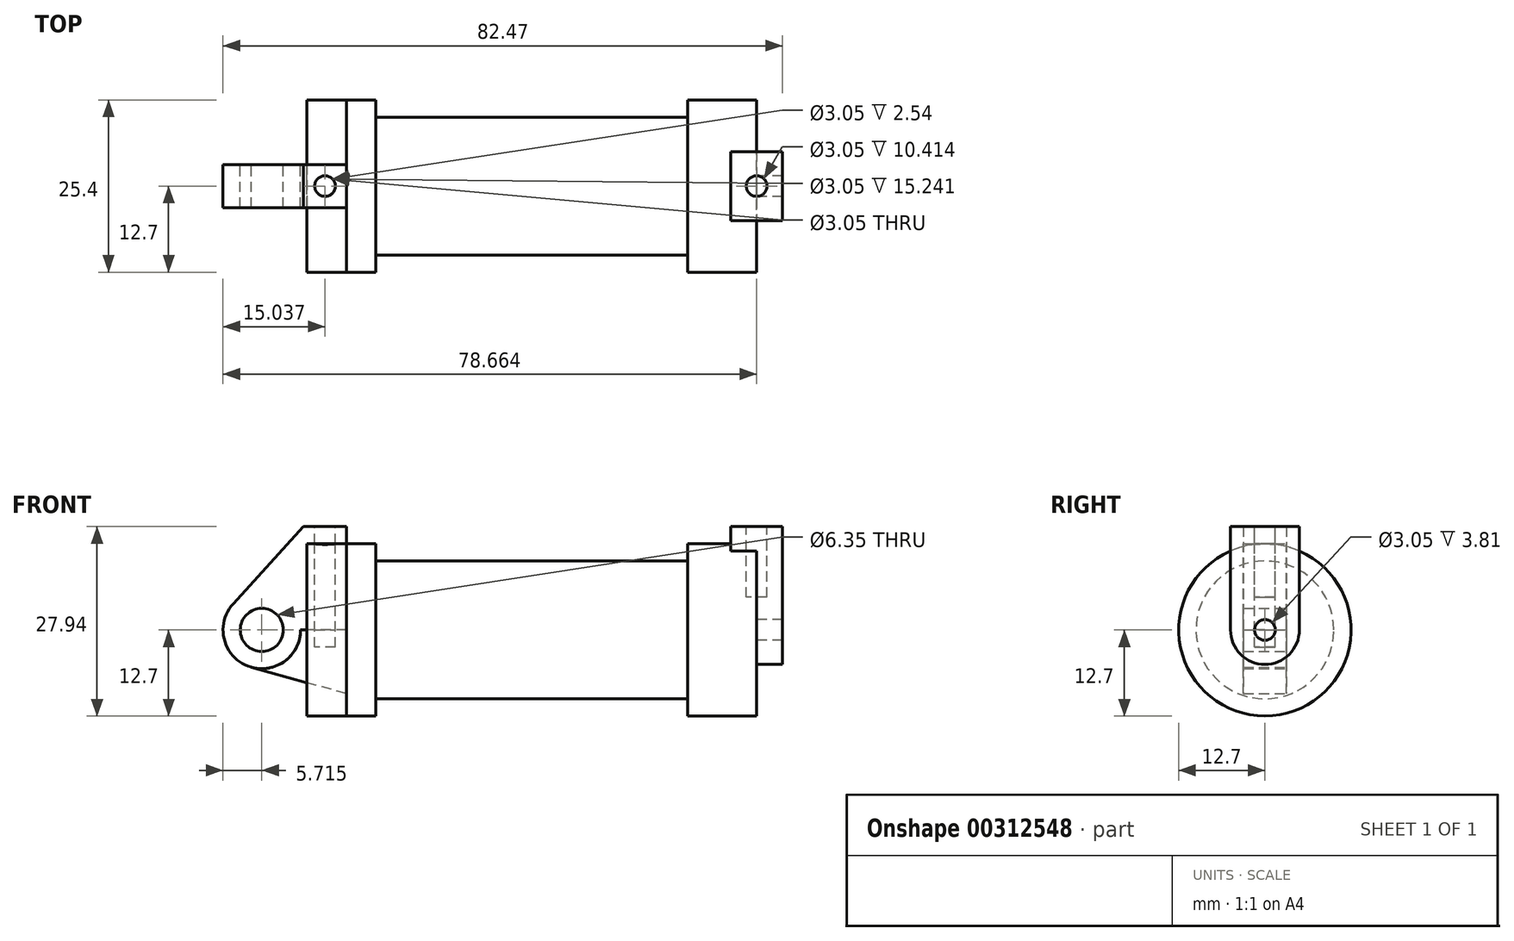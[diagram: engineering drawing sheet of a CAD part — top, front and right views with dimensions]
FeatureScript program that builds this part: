
annotation { "Feature Type Name" : "Feature", "Feature Type Description" : "" }
export const myFeature = defineFeature(function(context is Context, id is Id, definition is map)
    precondition{}
    {
        {
            var Q0;
            Q0=qCreatedBy(makeId("Front.planeOp"),FACE);
            var sketch = newSketch(context, id + "F0", { "sketchPlane" : qUnion([Q0])});
            skLineSegment(sketch, "E0", {"start": v(0, 0) * mm, "end": v(0, 12.7) * mm});
            skLineSegment(sketch, "E1", {"start": v(0, 12.7) * mm, "end": v(10.16, 12.7) * mm});
            skLineSegment(sketch, "E2", {"start": v(10.16, 12.7) * mm, "end": v(10.16, 10.16) * mm});
            skLineSegment(sketch, "E3", {"start": v(10.16, 10.16) * mm, "end": v(56.13, 10.16) * mm});
            skLineSegment(sketch, "E4", {"start": v(56.13, 10.16) * mm, "end": v(56.13, 12.7) * mm});
            skLineSegment(sketch, "E5", {"start": v(56.13, 12.7) * mm, "end": v(66.3, 12.7) * mm});
            skLineSegment(sketch, "E6", {"start": v(66.3, 12.7) * mm, "end": v(66.3, 0) * mm});
            skLineSegment(sketch, "E7", {"start": v(66.3, 0) * mm, "end": v(0, 0) * mm});
            skLineSegment(sketch, "E8", {"start": v(5.84, 15.24) * mm, "end": v(-0.5, 15.24) * mm});
            skLineSegment(sketch, "E9", {"start": v(-0.5, 15.24) * mm, "end": v(-10.88, 3.85) * mm});
            skLineSegment(sketch, "E10", {"start": v(0, 0) * mm, "end": v(-6.65, 0) * mm});
            skCircle(sketch, "E11", {"center": v(-6.65, 0) * mm, "radius": 5.72 * mm});
            skCircle(sketch, "E12", {"center": v(-6.65, 0) * mm, "radius": 3.18 * mm});
            skLineSegment(sketch, "E13", {"start": v(5.84, 15.24) * mm, "end": v(5.84, -9.4) * mm});
            skLineSegment(sketch, "E14", {"start": v(5.84, -9.4) * mm, "end": v(-8.18, -5.5) * mm});
            skSolve(sketch);
        }
        {
            var Q0;
            {var subQ1=sQuery(id+"F0.wireOp",EDGE,"E0");Q0=makeQuery(id+"F0.imprint","IMPRINT",FACE,{"disambiguationData":[TD([[makeQuery(id+"F0.imprint","IMPRINT",EDGE,{"derivedFrom":subQ1}),1.0]])]});}
            var Q1;
            Q1=makeQuery(id+"F0.imprint","IMPRINT",FACE,{"disambiguationData":[TD([[makeQuery(id+"F0.imprint","IMPRINT",EDGE,{"derivedFrom":sQuery(id+"F0.wireOp",EDGE,"E12")}),-1.0]])]});
            extrude(context, id + "F1", {"entities" : qUnion([Q0, Q1]), "endBound" : BoundingType.SYMMETRIC, "depth" : 6.35 * mm});
        }
        {
            var Q0;
            {var subQ0=sQuery(id+"F0.wireOp",EDGE,"E2");Q0=makeQuery(id+"F0.imprint","IMPRINT",FACE,{"disambiguationData":[TD([[makeQuery(id+"F0.imprint","IMPRINT",EDGE,{"derivedFrom":subQ0}),-1.0]])]});}
            var Q1;
            Q1=sQuery(id+"F0.wireOp",EDGE,"E10");
            revolve(context, id + "F2", {"entities" : qUnion([Q0]), "axis" : qUnion([Q1]), "revolveType" : RevolveType.TWO_DIRECTIONS, "angle" : 180 * degree, "angleBack" : 180 * degree});
        }
        {
            var Q0;
            {var subQ0=sQuery(id+"F0.wireOp",EDGE,"E0");Q0=makeQuery(id+"F0.imprint","IMPRINT",FACE,{"disambiguationData":[TD([[makeQuery(id+"F0.imprint","IMPRINT",EDGE,{"derivedFrom":subQ0}),-1.0]])]});}
            var Q1;
            Q1=sQuery(id+"F0.wireOp",EDGE,"E10");
            revolve(context, id + "F3", {"entities" : qUnion([Q0]), "axis" : qUnion([Q1]), "revolveType" : RevolveType.FULL});
        }
        {
            var Q0;
            {var subQ0=sQuery(id+"F0.wireOp",EDGE,"E14");Q0=makeQuery(id+"F0.imprint","IMPRINT",FACE,{"disambiguationData":[TD([[makeQuery(id+"F0.imprint","IMPRINT",EDGE,{"derivedFrom":subQ0}),-1.0]])]});}
            extrude(context, id + "F4", {"entities" : qUnion([Q0]), "endBound" : BoundingType.SYMMETRIC, "depth" : 6.35 * mm});
        }
        {
            var Q0;
            Q0=makeQuery(id+"F2.opRevolve","SWEPT_FACE",FACE,{"disambiguationData":[OSD([sQuery(id+"F0.wireOp",EDGE,"E6")])]});
            var sketch = newSketch(context, id + "F5", { "sketchPlane" : qUnion([Q0])});
            skCircle(sketch, "E15", {"center": v(0, 0) * mm, "radius": 5.08 * mm});
            skCircle(sketch, "E16", {"center": v(0, 0) * mm, "radius": 1.52 * mm});
            skLineSegment(sketch, "E17", {"start": v(5.08, 0) * mm, "end": v(5.08, 15.24) * mm});
            skLineSegment(sketch, "E18", {"start": v(-5.08, 0) * mm, "end": v(-5.08, 15.24) * mm});
            skLineSegment(sketch, "E19", {"start": v(-5.08, 15.24) * mm, "end": v(5.08, 15.24) * mm});
            skSolve(sketch);
        }
        {
            var Q0;
            Q0 = qSketchRegion(id + "F5", true);
            extrude(context, id + "F6", {"entities" : qUnion([Q0]), "operationType" : NewBodyOperationType.ADD, "endBound" : BoundingType.SYMMETRIC, "depth" : 7.62 * mm});
        }
        {
            var Q0;
            Q0=makeQuery(id+"F6.opExtrude","SWEPT_FACE",FACE,{"disambiguationData":[OSD([sQuery(id+"F5.wireOp",EDGE,"E19")])]});
            var sketch = newSketch(context, id + "F7", { "sketchPlane" : qUnion([Q0])});
            skCircle(sketch, "E20", {"center": v(66.3, 0) * mm, "radius": 1.52 * mm});
            skPoint(sketch, "E20.centerSnap0", {"position": v(70.1, 0) * mm});
            skPoint(sketch, "E20.centerSnap1", {"position": v(66.3, 5.08) * mm});
            skSolve(sketch);
        }
        {
            var Q0;
            Q0=makeQuery(id+"F7.imprint","IMPRINT",FACE,{"disambiguationData":[TD([[makeQuery(id+"F7.imprint","IMPRINT",EDGE,{"derivedFrom":sQuery(id+"F7.wireOp",EDGE,"E20")}),1.0]])]});
            var Q1;
            Q1=sQuery(id+"F7.wireOp",EDGE,"E20");
            extrude(context, id + "F8", {"entities" : qUnion([Q0]), "operationType" : NewBodyOperationType.REMOVE, "surfaceEntities" : qUnion([Q1]), "oppositeDirection" : true, "depth" : 10.4 * mm});
        }
        {
            var Q0;
            Q0=makeQuery(id+"F1.opExtrude","SWEPT_FACE",FACE,{"disambiguationData":[OSD([sQuery(id+"F0.wireOp",EDGE,"E8")])]});
            var sketch = newSketch(context, id + "F9", { "sketchPlane" : qUnion([Q0])});
            skCircle(sketch, "E21", {"center": v(2.67, 0) * mm, "radius": 1.52 * mm});
            skPoint(sketch, "E21.centerSnap0", {"position": v(5.84, 0) * mm});
            skPoint(sketch, "E21.centerSnap1", {"position": v(2.67, 3.18) * mm});
            skSolve(sketch);
        }
        {
            var Q0;
            Q0=makeQuery(id+"F9.imprint","IMPRINT",FACE,{"disambiguationData":[TD([[makeQuery(id+"F9.imprint","IMPRINT",EDGE,{"derivedFrom":sQuery(id+"F9.wireOp",EDGE,"E21")}),1.0]])]});
            extrude(context, id + "F10", {"entities" : qUnion([Q0]), "operationType" : NewBodyOperationType.REMOVE, "oppositeDirection" : true, "depth" : 17.78 * mm});
        }
    });
